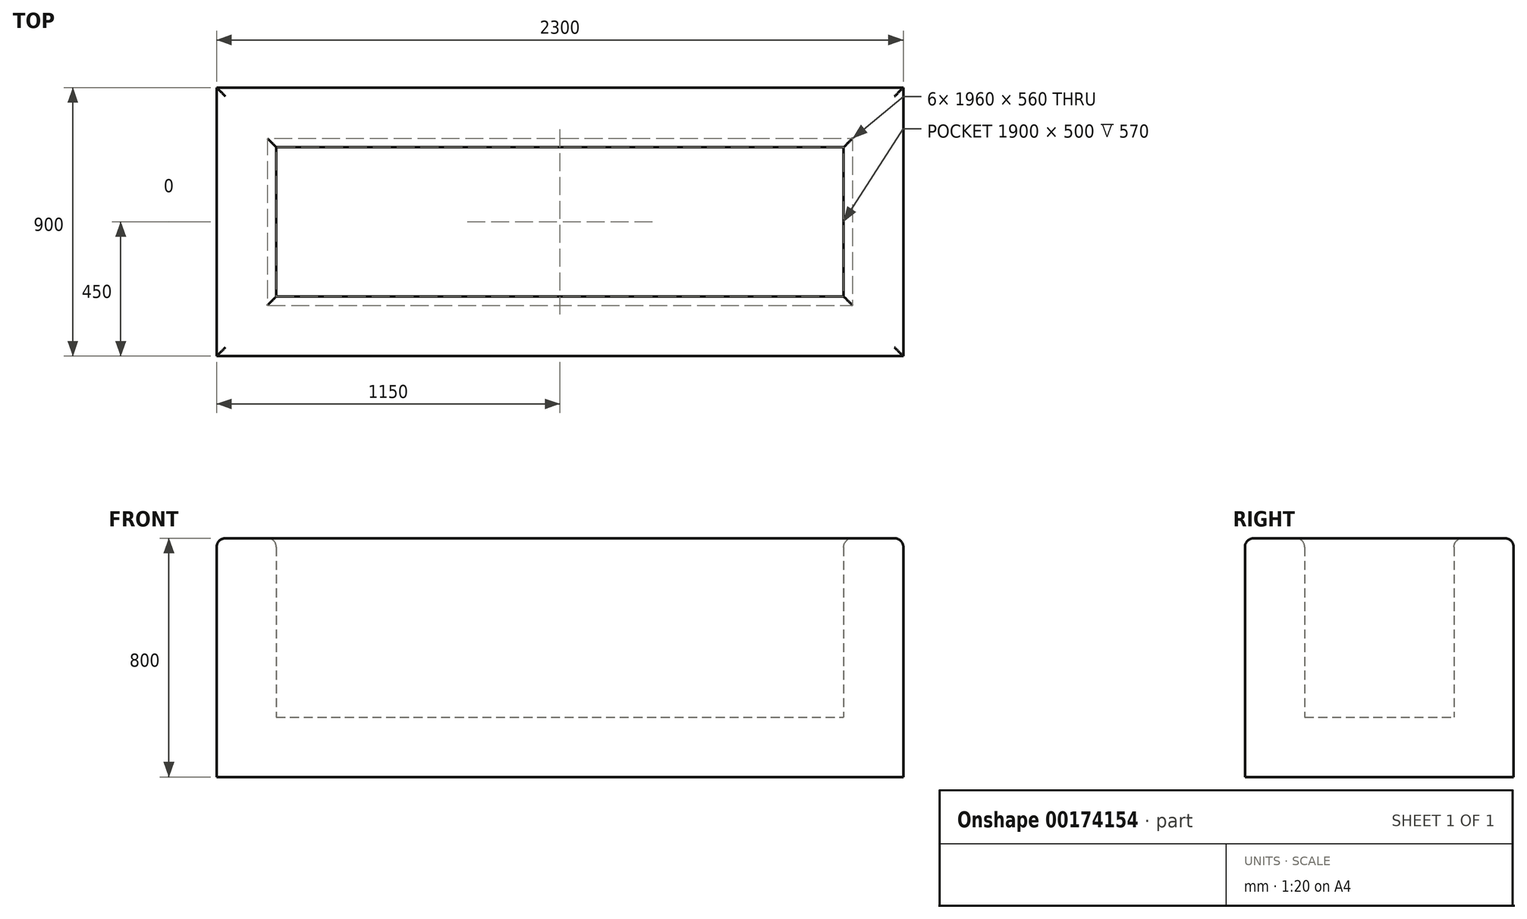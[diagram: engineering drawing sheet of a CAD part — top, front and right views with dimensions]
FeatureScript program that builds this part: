
annotation { "Feature Type Name" : "Feature", "Feature Type Description" : "" }
export const myFeature = defineFeature(function(context is Context, id is Id, definition is map)
    precondition{}
    {
        {
            var Q0;
            Q0=qCreatedBy(makeId("Top.planeOp"),FACE);
            var sketch = newSketch(context, id + "F0", { "sketchPlane" : qUnion([Q0])});
            skLineSegment(sketch, "E0.bottom", {"start": v(0, 0) * mm, "end": v(2300, 0) * mm});
            skLineSegment(sketch, "E0.top", {"start": v(0, 900) * mm, "end": v(2300, 900) * mm});
            skLineSegment(sketch, "E0.left", {"start": v(0, 0) * mm, "end": v(0, 900) * mm});
            skLineSegment(sketch, "E0.right", {"start": v(2300, 0) * mm, "end": v(2300, 900) * mm});
            skSolve(sketch);
        }
        {
            var Q0;
            Q0=makeQuery(id+"F0.imprint","IMPRINT",FACE,{"disambiguationData":[TD([[makeQuery(id+"F0.imprint","IMPRINT",EDGE,{"derivedFrom":sQuery(id+"F0.wireOp",EDGE,"E0.bottom")}),1.0]])]});
            extrude(context, id + "F1", {"entities" : qUnion([Q0]), "depth" : 800 * mm});
        }
        {
            var Q0;
            Q0=makeQuery(id+"F1.opExtrude","CAP_FACE",FACE,{"disambiguationData":[OSD([sQuery(id+"F0.wireOp",EDGE,"E0.bottom"),sQuery(id+"F0.wireOp",EDGE,"E0.top"),sQuery(id+"F0.wireOp",EDGE,"E0.left"),sQuery(id+"F0.wireOp",EDGE,"E0.right")])],"isStart":false});
            shell(context, id + "F2", {"entities" : qUnion([Q0]), "thickness" : 200 * mm});
        }
        {
            var Q0;
            Q0=makeQuery(id+"F1.opExtrude","CAP_EDGE",EDGE,{"disambiguationData":[OSD([sQuery(id+"F0.wireOp",EDGE,"E0.bottom")])],"isStart":false});
            var Q1;
            Q1=makeQuery(id+"F1.opExtrude","CAP_EDGE",EDGE,{"disambiguationData":[OSD([sQuery(id+"F0.wireOp",EDGE,"E0.left")])],"isStart":false});
            var Q2;
            {var subQ0=sQuery(id+"F0.wireOp",EDGE,"E0.left");Q2=makeQuery(id+"F2.opShell","OFFSET_EDGE",EDGE,{"disambiguationData":[OSD([subQ0]),TDD([makeQuery(id+"F1.opExtrude","CAP_EDGE",EDGE,{"disambiguationData":[OSD([subQ0])],"isStart":false})])]});}
            var Q3;
            {var subQ0=sQuery(id+"F0.wireOp",EDGE,"E0.bottom");Q3=makeQuery(id+"F2.opShell","OFFSET_EDGE",EDGE,{"disambiguationData":[OSD([subQ0]),TDD([makeQuery(id+"F1.opExtrude","CAP_EDGE",EDGE,{"disambiguationData":[OSD([subQ0])],"isStart":false})])]});}
            var Q4;
            {var subQ0=sQuery(id+"F0.wireOp",EDGE,"E0.top");Q4=makeQuery(id+"F2.opShell","OFFSET_EDGE",EDGE,{"disambiguationData":[OSD([subQ0]),TDD([makeQuery(id+"F1.opExtrude","CAP_EDGE",EDGE,{"disambiguationData":[OSD([subQ0])],"isStart":false})])]});}
            var Q5;
            Q5=makeQuery(id+"F1.opExtrude","CAP_EDGE",EDGE,{"disambiguationData":[OSD([sQuery(id+"F0.wireOp",EDGE,"E0.top")])],"isStart":false});
            var Q6;
            Q6=makeQuery(id+"F1.opExtrude","CAP_EDGE",EDGE,{"disambiguationData":[OSD([sQuery(id+"F0.wireOp",EDGE,"E0.right")])],"isStart":false});
            var Q7;
            {var subQ0=sQuery(id+"F0.wireOp",EDGE,"E0.right");Q7=makeQuery(id+"F2.opShell","OFFSET_EDGE",EDGE,{"disambiguationData":[OSD([subQ0]),TDD([makeQuery(id+"F1.opExtrude","CAP_EDGE",EDGE,{"disambiguationData":[OSD([subQ0])],"isStart":false})])]});}
            fillet(context, id + "F3", {"entities" : qUnion([Q0, Q1, Q2, Q3, Q4, Q5, Q6, Q7]), "radius" : 30 * mm, "tangentPropagation" : true, "allowEdgeOverflow" : false});
        }
    });
